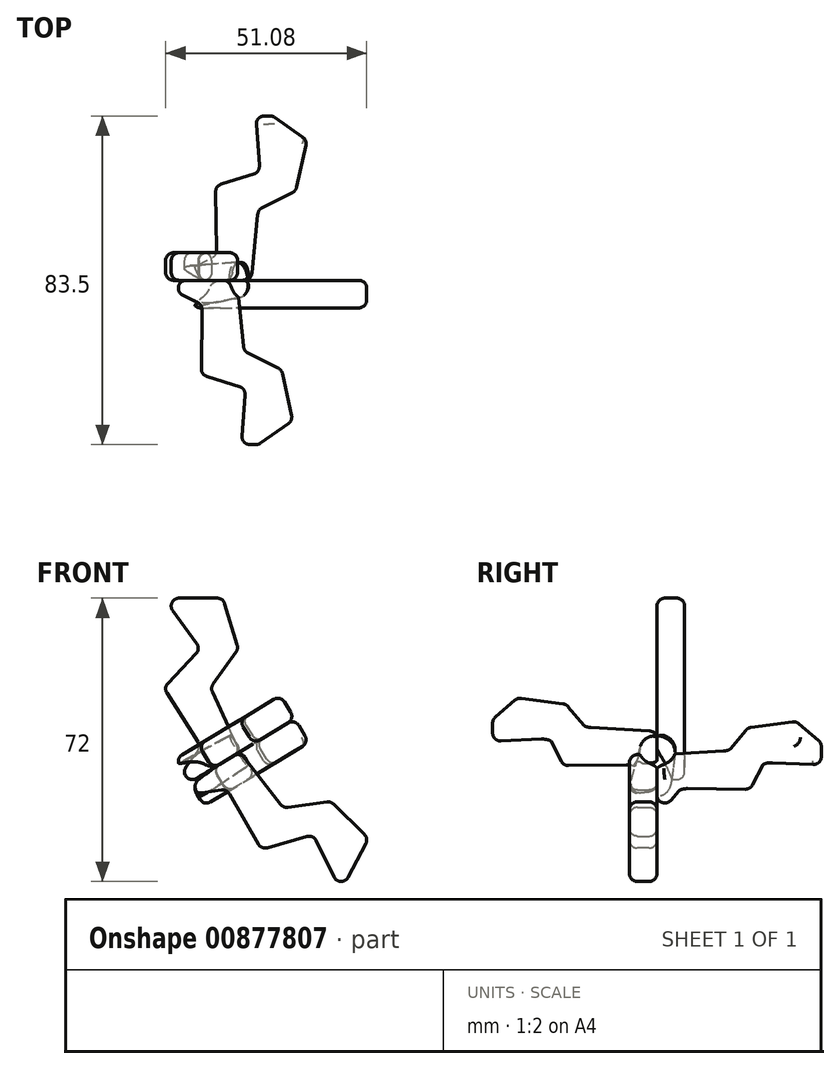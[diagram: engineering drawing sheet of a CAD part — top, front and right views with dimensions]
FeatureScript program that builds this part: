
annotation { "Feature Type Name" : "Feature", "Feature Type Description" : "" }
export const myFeature = defineFeature(function(context is Context, id is Id, definition is map)
    precondition{}
    {
        {
            var Q0;
            Q0=qCreatedBy(makeId("Front.planeOp"),FACE);
            var sketch = newSketch(context, id + "F0", { "sketchPlane" : qUnion([Q0])});
            skLineSegment(sketch, "E0", {"start": v(-48.1, 12.9) * mm, "end": v(-32.98, 12.9) * mm});
            skLineSegment(sketch, "E1", {"start": v(-48.1, 12.9) * mm, "end": v(-38.67, 0) * mm});
            skLineSegment(sketch, "E2", {"start": v(-38.67, 0) * mm, "end": v(-48.1, -9.87) * mm});
            skLineSegment(sketch, "E3", {"start": v(-48.1, -9.87) * mm, "end": v(-38.67, -24.8) * mm});
            skLineSegment(sketch, "E4", {"start": v(-38.67, -24.8) * mm, "end": v(-48.1, -37.96) * mm});
            skLineSegment(sketch, "E5", {"start": v(-48.1, -37.96) * mm, "end": v(-28.71, -26.23) * mm});
            skLineSegment(sketch, "E6", {"start": v(-28.71, -26.23) * mm, "end": v(-36.18, -9.87) * mm});
            skLineSegment(sketch, "E7", {"start": v(-36.18, -9.87) * mm, "end": v(-29.11, 0) * mm});
            skLineSegment(sketch, "E8", {"start": v(-29.11, 0) * mm, "end": v(-32.98, 12.9) * mm});
            skSolve(sketch);
        }
        {
            var Q0;
            Q0=makeQuery(id+"F0.imprint","IMPRINT",FACE,{"disambiguationData":[TD([[makeQuery(id+"F0.imprint","IMPRINT",EDGE,{"derivedFrom":sQuery(id+"F0.wireOp",EDGE,"E0")}),-1.0]])]});
            extrude(context, id + "F1", {"entities" : qUnion([Q0]), "depth" : 7 * mm, "offsetDistance" : 25.4 * mm});
        }
        {
            var Q0;
            Q0=makeQuery(id+"F1.opExtrude","SWEPT_BODY",BODY,{"disambiguationData":[OSD([sQuery(id+"F0.wireOp",EDGE,"E0"),sQuery(id+"F0.wireOp",EDGE,"E1"),sQuery(id+"F0.wireOp",EDGE,"E2"),sQuery(id+"F0.wireOp",EDGE,"E3"),sQuery(id+"F0.wireOp",EDGE,"E4"),sQuery(id+"F0.wireOp",EDGE,"E5"),sQuery(id+"F0.wireOp",EDGE,"E6"),sQuery(id+"F0.wireOp",EDGE,"E7"),sQuery(id+"F0.wireOp",EDGE,"E8")])]});
            var Q1;
            Q1=makeQuery(id+"F1.opExtrude","CAP_EDGE",EDGE,{"disambiguationData":[OSD([sQuery(id+"F0.wireOp",EDGE,"E5")])],"isStart":false});
            circularPattern(context, id + "F2", {"entities" : qUnion([Q0]), "axis" : qUnion([Q1]), "angle" : 360 * degree, "instanceCount" : 4, "equalSpace" : true});
        }
        {
            var Q0;
            Q0=makeQuery(id+"F1.opExtrude","SWEPT_FACE",FACE,{"disambiguationData":[OSD([sQuery(id+"F0.wireOp",EDGE,"E0")])]});
            var Q1;
            Q1=makeQuery(id+"F1.opExtrude","SWEPT_FACE",FACE,{"disambiguationData":[OSD([sQuery(id+"F0.wireOp",EDGE,"E8")])]});
            var Q2;
            Q2=makeQuery(id+"F1.opExtrude","SWEPT_FACE",FACE,{"disambiguationData":[OSD([sQuery(id+"F0.wireOp",EDGE,"E7")])]});
            var Q3;
            Q3=makeQuery(id+"F2.opPattern","COPY",FACE,{"derivedFrom":makeQuery(id+"F1.opExtrude","SWEPT_FACE",FACE,{"disambiguationData":[OSD([sQuery(id+"F0.wireOp",EDGE,"E6")])]}),"instanceName":"1"});
            var Q4;
            Q4=makeQuery(id+"F2.opPattern","COPY",FACE,{"derivedFrom":makeQuery(id+"F1.opExtrude","SWEPT_FACE",FACE,{"disambiguationData":[OSD([sQuery(id+"F0.wireOp",EDGE,"E8")])]}),"instanceName":"1"});
            var Q5;
            Q5=makeQuery(id+"F2.opPattern","COPY",EDGE,{"derivedFrom":makeQuery(id+"F1.opExtrude","SWEPT_EDGE",EDGE,{"disambiguationData":[OSD([sQuery(id+"F0.wireOp",EDGE,"E0"),sQuery(id+"F0.wireOp",EDGE,"E1")])]}),"instanceName":"1"});
            var Q6;
            Q6=makeQuery(id+"F2.opPattern","COPY",FACE,{"derivedFrom":makeQuery(id+"F1.opExtrude","SWEPT_FACE",FACE,{"disambiguationData":[OSD([sQuery(id+"F0.wireOp",EDGE,"E8")])]}),"instanceName":"2"});
            var Q7;
            Q7=makeQuery(id+"F2.opPattern","COPY",FACE,{"derivedFrom":makeQuery(id+"F1.opExtrude","SWEPT_FACE",FACE,{"disambiguationData":[OSD([sQuery(id+"F0.wireOp",EDGE,"E0")])]}),"instanceName":"2"});
            var Q8;
            Q8=makeQuery(id+"F2.opPattern","COPY",FACE,{"derivedFrom":makeQuery(id+"F1.opExtrude","SWEPT_FACE",FACE,{"disambiguationData":[OSD([sQuery(id+"F0.wireOp",EDGE,"E0")])]}),"instanceName":"1"});
            var Q9;
            Q9=makeQuery(id+"F2.opPattern","COPY",FACE,{"derivedFrom":makeQuery(id+"F1.opExtrude","SWEPT_FACE",FACE,{"disambiguationData":[OSD([sQuery(id+"F0.wireOp",EDGE,"E6")])]}),"instanceName":"2"});
            var Q10;
            Q10=makeQuery(id+"F2.opPattern","COPY",FACE,{"derivedFrom":makeQuery(id+"F1.opExtrude","SWEPT_FACE",FACE,{"disambiguationData":[OSD([sQuery(id+"F0.wireOp",EDGE,"E6")])]}),"instanceName":"3"});
            var Q11;
            Q11=makeQuery(id+"F2.opPattern","COPY",FACE,{"derivedFrom":makeQuery(id+"F1.opExtrude","SWEPT_FACE",FACE,{"disambiguationData":[OSD([sQuery(id+"F0.wireOp",EDGE,"E7")])]}),"instanceName":"3"});
            var Q12;
            Q12=makeQuery(id+"F2.opPattern","COPY",FACE,{"derivedFrom":makeQuery(id+"F1.opExtrude","SWEPT_FACE",FACE,{"disambiguationData":[OSD([sQuery(id+"F0.wireOp",EDGE,"E8")])]}),"instanceName":"3"});
            var Q13;
            Q13=makeQuery(id+"F2.opPattern","COPY",EDGE,{"derivedFrom":makeQuery(id+"F1.opExtrude","SWEPT_EDGE",EDGE,{"disambiguationData":[OSD([sQuery(id+"F0.wireOp",EDGE,"E0"),sQuery(id+"F0.wireOp",EDGE,"E1")])]}),"instanceName":"3"});
            var Q14;
            Q14=makeQuery(id+"F2.opPattern","COPY",FACE,{"derivedFrom":makeQuery(id+"F1.opExtrude","CAP_FACE",FACE,{"disambiguationData":[OSD([sQuery(id+"F0.wireOp",EDGE,"E0"),sQuery(id+"F0.wireOp",EDGE,"E1"),sQuery(id+"F0.wireOp",EDGE,"E2"),sQuery(id+"F0.wireOp",EDGE,"E3"),sQuery(id+"F0.wireOp",EDGE,"E4"),sQuery(id+"F0.wireOp",EDGE,"E5"),sQuery(id+"F0.wireOp",EDGE,"E6"),sQuery(id+"F0.wireOp",EDGE,"E7"),sQuery(id+"F0.wireOp",EDGE,"E8")])],"isStart":false}),"instanceName":"2"});
            var Q15;
            Q15=makeQuery(id+"F2.opPattern","COPY",EDGE,{"derivedFrom":makeQuery(id+"F1.opExtrude","CAP_EDGE",EDGE,{"disambiguationData":[OSD([sQuery(id+"F0.wireOp",EDGE,"E1")])],"isStart":false}),"instanceName":"1"});
            var Q16;
            Q16=makeQuery(id+"F1.opExtrude","CAP_FACE",FACE,{"disambiguationData":[OSD([sQuery(id+"F0.wireOp",EDGE,"E0"),sQuery(id+"F0.wireOp",EDGE,"E1"),sQuery(id+"F0.wireOp",EDGE,"E2"),sQuery(id+"F0.wireOp",EDGE,"E3"),sQuery(id+"F0.wireOp",EDGE,"E4"),sQuery(id+"F0.wireOp",EDGE,"E5"),sQuery(id+"F0.wireOp",EDGE,"E6"),sQuery(id+"F0.wireOp",EDGE,"E7"),sQuery(id+"F0.wireOp",EDGE,"E8")])],"isStart":true});
            var Q17;
            Q17=makeQuery(id+"F2.opPattern","COPY",FACE,{"derivedFrom":makeQuery(id+"F1.opExtrude","CAP_FACE",FACE,{"disambiguationData":[OSD([sQuery(id+"F0.wireOp",EDGE,"E0"),sQuery(id+"F0.wireOp",EDGE,"E1"),sQuery(id+"F0.wireOp",EDGE,"E2"),sQuery(id+"F0.wireOp",EDGE,"E3"),sQuery(id+"F0.wireOp",EDGE,"E4"),sQuery(id+"F0.wireOp",EDGE,"E5"),sQuery(id+"F0.wireOp",EDGE,"E6"),sQuery(id+"F0.wireOp",EDGE,"E7"),sQuery(id+"F0.wireOp",EDGE,"E8")])],"isStart":true}),"instanceName":"3"});
            var Q18;
            Q18=makeQuery(id+"F1.opExtrude","CAP_FACE",FACE,{"disambiguationData":[OSD([sQuery(id+"F0.wireOp",EDGE,"E0"),sQuery(id+"F0.wireOp",EDGE,"E1"),sQuery(id+"F0.wireOp",EDGE,"E2"),sQuery(id+"F0.wireOp",EDGE,"E3"),sQuery(id+"F0.wireOp",EDGE,"E4"),sQuery(id+"F0.wireOp",EDGE,"E5"),sQuery(id+"F0.wireOp",EDGE,"E6"),sQuery(id+"F0.wireOp",EDGE,"E7"),sQuery(id+"F0.wireOp",EDGE,"E8")])],"isStart":false});
            var Q19;
            Q19=makeQuery(id+"F2.opPattern","COPY",FACE,{"derivedFrom":makeQuery(id+"F1.opExtrude","CAP_FACE",FACE,{"disambiguationData":[OSD([sQuery(id+"F0.wireOp",EDGE,"E0"),sQuery(id+"F0.wireOp",EDGE,"E1"),sQuery(id+"F0.wireOp",EDGE,"E2"),sQuery(id+"F0.wireOp",EDGE,"E3"),sQuery(id+"F0.wireOp",EDGE,"E4"),sQuery(id+"F0.wireOp",EDGE,"E5"),sQuery(id+"F0.wireOp",EDGE,"E6"),sQuery(id+"F0.wireOp",EDGE,"E7"),sQuery(id+"F0.wireOp",EDGE,"E8")])],"isStart":true}),"instanceName":"1"});
            var Q20;
            Q20=makeQuery(id+"F2.opPattern","COPY",FACE,{"derivedFrom":makeQuery(id+"F1.opExtrude","CAP_FACE",FACE,{"disambiguationData":[OSD([sQuery(id+"F0.wireOp",EDGE,"E0"),sQuery(id+"F0.wireOp",EDGE,"E1"),sQuery(id+"F0.wireOp",EDGE,"E2"),sQuery(id+"F0.wireOp",EDGE,"E3"),sQuery(id+"F0.wireOp",EDGE,"E4"),sQuery(id+"F0.wireOp",EDGE,"E5"),sQuery(id+"F0.wireOp",EDGE,"E6"),sQuery(id+"F0.wireOp",EDGE,"E7"),sQuery(id+"F0.wireOp",EDGE,"E8")])],"isStart":false}),"instanceName":"1"});
            var Q21;
            Q21=makeQuery(id+"F2.opPattern","COPY",EDGE,{"derivedFrom":makeQuery(id+"F1.opExtrude","CAP_EDGE",EDGE,{"disambiguationData":[OSD([sQuery(id+"F0.wireOp",EDGE,"E8")])],"isStart":false}),"instanceName":"1"});
            var Q22;
            Q22=makeQuery(id+"F2.opPattern","COPY",EDGE,{"derivedFrom":makeQuery(id+"F1.opExtrude","CAP_EDGE",EDGE,{"disambiguationData":[OSD([sQuery(id+"F0.wireOp",EDGE,"E0")])],"isStart":false}),"instanceName":"1"});
            var Q23;
            Q23=makeQuery(id+"F2.opPattern","COPY",EDGE,{"derivedFrom":makeQuery(id+"F1.opExtrude","SWEPT_EDGE",EDGE,{"disambiguationData":[OSD([sQuery(id+"F0.wireOp",EDGE,"E6"),sQuery(id+"F0.wireOp",EDGE,"E7")])]}),"instanceName":"1"});
            var Q24;
            Q24=makeQuery(id+"F2.opPattern","COPY",EDGE,{"derivedFrom":makeQuery(id+"F1.opExtrude","CAP_EDGE",EDGE,{"disambiguationData":[OSD([sQuery(id+"F0.wireOp",EDGE,"E6")])],"isStart":true}),"instanceName":"1"});
            var Q25;
            Q25=makeQuery(id+"F2.opPattern","COPY",EDGE,{"derivedFrom":makeQuery(id+"F1.opExtrude","SWEPT_EDGE",EDGE,{"disambiguationData":[OSD([sQuery(id+"F0.wireOp",EDGE,"E0"),sQuery(id+"F0.wireOp",EDGE,"E8")])]}),"instanceName":"1"});
            var Q26;
            Q26=makeQuery(id+"F2.opPattern","COPY",EDGE,{"derivedFrom":makeQuery(id+"F1.opExtrude","CAP_EDGE",EDGE,{"disambiguationData":[OSD([sQuery(id+"F0.wireOp",EDGE,"E6")])],"isStart":false}),"instanceName":"1"});
            var Q27;
            Q27=makeQuery(id+"F2.opPattern","COPY",EDGE,{"derivedFrom":makeQuery(id+"F1.opExtrude","CAP_EDGE",EDGE,{"disambiguationData":[OSD([sQuery(id+"F0.wireOp",EDGE,"E8")])],"isStart":true}),"instanceName":"1"});
            var Q28;
            Q28=makeQuery(id+"F2.opPattern","COPY",EDGE,{"derivedFrom":makeQuery(id+"F1.opExtrude","SWEPT_EDGE",EDGE,{"disambiguationData":[OSD([sQuery(id+"F0.wireOp",EDGE,"E7"),sQuery(id+"F0.wireOp",EDGE,"E8")])]}),"instanceName":"1"});
            var Q29;
            Q29=makeQuery(id+"F2.opPattern","COPY",EDGE,{"derivedFrom":makeQuery(id+"F1.opExtrude","CAP_EDGE",EDGE,{"disambiguationData":[OSD([sQuery(id+"F0.wireOp",EDGE,"E6")])],"isStart":false}),"instanceName":"2"});
            var Q30;
            Q30=makeQuery(id+"F2.opPattern","COPY",EDGE,{"derivedFrom":makeQuery(id+"F1.opExtrude","CAP_EDGE",EDGE,{"disambiguationData":[OSD([sQuery(id+"F0.wireOp",EDGE,"E4")])],"isStart":false}),"instanceName":"2"});
            var Q31;
            Q31=makeQuery(id+"F2.opPattern","COPY",EDGE,{"derivedFrom":makeQuery(id+"F1.opExtrude","CAP_EDGE",EDGE,{"disambiguationData":[OSD([sQuery(id+"F0.wireOp",EDGE,"E0")])],"isStart":true}),"instanceName":"2"});
            var Q32;
            Q32=makeQuery(id+"F2.opPattern","COPY",EDGE,{"derivedFrom":makeQuery(id+"F1.opExtrude","SWEPT_EDGE",EDGE,{"disambiguationData":[OSD([sQuery(id+"F0.wireOp",EDGE,"E4"),sQuery(id+"F0.wireOp",EDGE,"E5")])]}),"instanceName":"2"});
            var Q33;
            Q33=makeQuery(id+"F2.opPattern","COPY",EDGE,{"derivedFrom":makeQuery(id+"F1.opExtrude","CAP_EDGE",EDGE,{"disambiguationData":[OSD([sQuery(id+"F0.wireOp",EDGE,"E0")])],"isStart":false}),"instanceName":"2"});
            var Q34;
            Q34=makeQuery(id+"F2.opPattern","COPY",EDGE,{"derivedFrom":makeQuery(id+"F1.opExtrude","SWEPT_EDGE",EDGE,{"disambiguationData":[OSD([sQuery(id+"F0.wireOp",EDGE,"E0"),sQuery(id+"F0.wireOp",EDGE,"E1")])]}),"instanceName":"2"});
            var Q35;
            Q35=makeQuery(id+"F2.opPattern","COPY",EDGE,{"derivedFrom":makeQuery(id+"F1.opExtrude","SWEPT_EDGE",EDGE,{"disambiguationData":[OSD([sQuery(id+"F0.wireOp",EDGE,"E2"),sQuery(id+"F0.wireOp",EDGE,"E3")])]}),"instanceName":"2"});
            var Q36;
            Q36=makeQuery(id+"F2.opPattern","COPY",EDGE,{"derivedFrom":makeQuery(id+"F1.opExtrude","SWEPT_EDGE",EDGE,{"disambiguationData":[OSD([sQuery(id+"F0.wireOp",EDGE,"E5"),sQuery(id+"F0.wireOp",EDGE,"E6")])]}),"instanceName":"2"});
            var Q37;
            Q37=makeQuery(id+"F2.opPattern","COPY",EDGE,{"derivedFrom":makeQuery(id+"F1.opExtrude","CAP_EDGE",EDGE,{"disambiguationData":[OSD([sQuery(id+"F0.wireOp",EDGE,"E4")])],"isStart":true}),"instanceName":"2"});
            var Q38;
            Q38=makeQuery(id+"F2.opPattern","COPY",EDGE,{"derivedFrom":makeQuery(id+"F1.opExtrude","CAP_EDGE",EDGE,{"disambiguationData":[OSD([sQuery(id+"F0.wireOp",EDGE,"E7")])],"isStart":false}),"instanceName":"2"});
            var Q39;
            Q39=makeQuery(id+"F2.opPattern","COPY",EDGE,{"derivedFrom":makeQuery(id+"F1.opExtrude","CAP_EDGE",EDGE,{"disambiguationData":[OSD([sQuery(id+"F0.wireOp",EDGE,"E2")])],"isStart":true}),"instanceName":"2"});
            var Q40;
            Q40=makeQuery(id+"F1.opExtrude","CAP_EDGE",EDGE,{"disambiguationData":[OSD([sQuery(id+"F0.wireOp",EDGE,"E5")])],"isStart":true});
            var Q41;
            Q41=makeQuery(id+"F1.opExtrude","SWEPT_EDGE",EDGE,{"disambiguationData":[OSD([sQuery(id+"F0.wireOp",EDGE,"E4"),sQuery(id+"F0.wireOp",EDGE,"E5")])]});
            var Q42;
            Q42=makeQuery(id+"F1.opExtrude","CAP_EDGE",EDGE,{"disambiguationData":[OSD([sQuery(id+"F0.wireOp",EDGE,"E4")])],"isStart":true});
            var Q43;
            Q43=makeQuery(id+"F1.opExtrude","SWEPT_EDGE",EDGE,{"disambiguationData":[OSD([sQuery(id+"F0.wireOp",EDGE,"E2"),sQuery(id+"F0.wireOp",EDGE,"E3")])]});
            var Q44;
            Q44=makeQuery(id+"F1.opExtrude","SWEPT_EDGE",EDGE,{"disambiguationData":[OSD([sQuery(id+"F0.wireOp",EDGE,"E3"),sQuery(id+"F0.wireOp",EDGE,"E4")])]});
            var Q45;
            Q45=makeQuery(id+"F1.opExtrude","SWEPT_EDGE",EDGE,{"disambiguationData":[OSD([sQuery(id+"F0.wireOp",EDGE,"E6"),sQuery(id+"F0.wireOp",EDGE,"E7")])]});
            var Q46;
            Q46=makeQuery(id+"F1.opExtrude","CAP_EDGE",EDGE,{"disambiguationData":[OSD([sQuery(id+"F0.wireOp",EDGE,"E5")])],"isStart":false});
            var Q47;
            Q47=makeQuery(id+"F2.opPattern","COPY",EDGE,{"derivedFrom":makeQuery(id+"F1.opExtrude","SWEPT_EDGE",EDGE,{"disambiguationData":[OSD([sQuery(id+"F0.wireOp",EDGE,"E4"),sQuery(id+"F0.wireOp",EDGE,"E5")])]}),"instanceName":"3"});
            var Q48;
            Q48=makeQuery(id+"F2.opPattern","COPY",EDGE,{"derivedFrom":makeQuery(id+"F1.opExtrude","CAP_EDGE",EDGE,{"disambiguationData":[OSD([sQuery(id+"F0.wireOp",EDGE,"E6")])],"isStart":false}),"instanceName":"3"});
            var Q49;
            Q49=makeQuery(id+"F2.opPattern","COPY",EDGE,{"derivedFrom":makeQuery(id+"F1.opExtrude","SWEPT_EDGE",EDGE,{"disambiguationData":[OSD([sQuery(id+"F0.wireOp",EDGE,"E3"),sQuery(id+"F0.wireOp",EDGE,"E4")])]}),"instanceName":"3"});
            var Q50;
            Q50=makeQuery(id+"F2.opPattern","COPY",EDGE,{"derivedFrom":makeQuery(id+"F1.opExtrude","CAP_EDGE",EDGE,{"disambiguationData":[OSD([sQuery(id+"F0.wireOp",EDGE,"E3")])],"isStart":true}),"instanceName":"3"});
            var Q51;
            Q51=makeQuery(id+"F2.opPattern","COPY",EDGE,{"derivedFrom":makeQuery(id+"F1.opExtrude","CAP_EDGE",EDGE,{"disambiguationData":[OSD([sQuery(id+"F0.wireOp",EDGE,"E6")])],"isStart":true}),"instanceName":"3"});
            var Q52;
            Q52=makeQuery(id+"F2.opPattern","COPY",EDGE,{"derivedFrom":makeQuery(id+"F1.opExtrude","CAP_EDGE",EDGE,{"disambiguationData":[OSD([sQuery(id+"F0.wireOp",EDGE,"E4")])],"isStart":false}),"instanceName":"3"});
            var Q53;
            Q53=makeQuery(id+"F2.opPattern","COPY",EDGE,{"derivedFrom":makeQuery(id+"F1.opExtrude","CAP_EDGE",EDGE,{"disambiguationData":[OSD([sQuery(id+"F0.wireOp",EDGE,"E7")])],"isStart":true}),"instanceName":"3"});
            var Q54;
            Q54=makeQuery(id+"F2.opPattern","COPY",EDGE,{"derivedFrom":makeQuery(id+"F1.opExtrude","SWEPT_EDGE",EDGE,{"disambiguationData":[OSD([sQuery(id+"F0.wireOp",EDGE,"E2"),sQuery(id+"F0.wireOp",EDGE,"E3")])]}),"instanceName":"3"});
            var Q55;
            Q55=makeQuery(id+"F2.opPattern","COPY",EDGE,{"derivedFrom":makeQuery(id+"F1.opExtrude","SWEPT_EDGE",EDGE,{"disambiguationData":[OSD([sQuery(id+"F0.wireOp",EDGE,"E5"),sQuery(id+"F0.wireOp",EDGE,"E6")])]}),"instanceName":"3"});
            var Q56;
            Q56=makeQuery(id+"F2.opPattern","COPY",EDGE,{"derivedFrom":makeQuery(id+"F1.opExtrude","SWEPT_EDGE",EDGE,{"disambiguationData":[OSD([sQuery(id+"F0.wireOp",EDGE,"E6"),sQuery(id+"F0.wireOp",EDGE,"E7")])]}),"instanceName":"3"});
            var Q57;
            Q57=makeQuery(id+"F2.opPattern","COPY",EDGE,{"derivedFrom":makeQuery(id+"F1.opExtrude","CAP_EDGE",EDGE,{"disambiguationData":[OSD([sQuery(id+"F0.wireOp",EDGE,"E5")])],"isStart":true}),"instanceName":"3"});
            var Q58;
            Q58=makeQuery(id+"F2.opPattern","COPY",EDGE,{"derivedFrom":makeQuery(id+"F1.opExtrude","CAP_EDGE",EDGE,{"disambiguationData":[OSD([sQuery(id+"F0.wireOp",EDGE,"E2")])],"isStart":true}),"instanceName":"3"});
            var Q59;
            Q59=makeQuery(id+"F2.opPattern","COPY",EDGE,{"derivedFrom":makeQuery(id+"F1.opExtrude","CAP_EDGE",EDGE,{"disambiguationData":[OSD([sQuery(id+"F0.wireOp",EDGE,"E4")])],"isStart":true}),"instanceName":"3"});
            var Q60;
            Q60=makeQuery(id+"F2.opPattern","COPY",EDGE,{"derivedFrom":makeQuery(id+"F1.opExtrude","SWEPT_EDGE",EDGE,{"disambiguationData":[OSD([sQuery(id+"F0.wireOp",EDGE,"E5"),sQuery(id+"F0.wireOp",EDGE,"E6")])]}),"instanceName":"1"});
            var Q61;
            Q61=makeQuery(id+"F2.opPattern","COPY",EDGE,{"derivedFrom":makeQuery(id+"F1.opExtrude","CAP_EDGE",EDGE,{"disambiguationData":[OSD([sQuery(id+"F0.wireOp",EDGE,"E7")])],"isStart":true}),"instanceName":"1"});
            var Q62;
            Q62=makeQuery(id+"F2.opPattern","COPY",EDGE,{"derivedFrom":makeQuery(id+"F1.opExtrude","CAP_EDGE",EDGE,{"disambiguationData":[OSD([sQuery(id+"F0.wireOp",EDGE,"E5")])],"isStart":true}),"instanceName":"1"});
            var Q63;
            Q63=makeQuery(id+"F2.opPattern","COPY",EDGE,{"derivedFrom":makeQuery(id+"F1.opExtrude","CAP_EDGE",EDGE,{"disambiguationData":[OSD([sQuery(id+"F0.wireOp",EDGE,"E7")])],"isStart":false}),"instanceName":"1"});
            var Q64;
            Q64=makeQuery(id+"F2.opPattern","COPY",EDGE,{"derivedFrom":makeQuery(id+"F1.opExtrude","CAP_EDGE",EDGE,{"disambiguationData":[OSD([sQuery(id+"F0.wireOp",EDGE,"E5")])],"isStart":false}),"instanceName":"1"});
            var Q65;
            Q65=makeQuery(id+"F2.opPattern","COPY",EDGE,{"derivedFrom":makeQuery(id+"F1.opExtrude","CAP_EDGE",EDGE,{"disambiguationData":[OSD([sQuery(id+"F0.wireOp",EDGE,"E2")])],"isStart":true}),"instanceName":"1"});
            var Q66;
            Q66=makeQuery(id+"F2.opPattern","COPY",EDGE,{"derivedFrom":makeQuery(id+"F1.opExtrude","CAP_EDGE",EDGE,{"disambiguationData":[OSD([sQuery(id+"F0.wireOp",EDGE,"E1")])],"isStart":true}),"instanceName":"1"});
            var Q67;
            Q67=makeQuery(id+"F2.opPattern","COPY",EDGE,{"derivedFrom":makeQuery(id+"F1.opExtrude","CAP_EDGE",EDGE,{"disambiguationData":[OSD([sQuery(id+"F0.wireOp",EDGE,"E3")])],"isStart":true}),"instanceName":"1"});
            var Q68;
            Q68=makeQuery(id+"F2.opPattern","COPY",EDGE,{"derivedFrom":makeQuery(id+"F1.opExtrude","SWEPT_EDGE",EDGE,{"disambiguationData":[OSD([sQuery(id+"F0.wireOp",EDGE,"E2"),sQuery(id+"F0.wireOp",EDGE,"E3")])]}),"instanceName":"1"});
            var Q69;
            Q69=makeQuery(id+"F2.opPattern","COPY",EDGE,{"derivedFrom":makeQuery(id+"F1.opExtrude","CAP_EDGE",EDGE,{"disambiguationData":[OSD([sQuery(id+"F0.wireOp",EDGE,"E0")])],"isStart":true}),"instanceName":"1"});
            var Q70;
            Q70=makeQuery(id+"F2.opPattern","COPY",EDGE,{"derivedFrom":makeQuery(id+"F1.opExtrude","SWEPT_EDGE",EDGE,{"disambiguationData":[OSD([sQuery(id+"F0.wireOp",EDGE,"E1"),sQuery(id+"F0.wireOp",EDGE,"E2")])]}),"instanceName":"1"});
            var Q71;
            Q71=makeQuery(id+"F2.opPattern","COPY",EDGE,{"derivedFrom":makeQuery(id+"F1.opExtrude","CAP_EDGE",EDGE,{"disambiguationData":[OSD([sQuery(id+"F0.wireOp",EDGE,"E3")])],"isStart":false}),"instanceName":"1"});
            var Q72;
            Q72=makeQuery(id+"F2.opPattern","COPY",EDGE,{"derivedFrom":makeQuery(id+"F1.opExtrude","SWEPT_EDGE",EDGE,{"disambiguationData":[OSD([sQuery(id+"F0.wireOp",EDGE,"E3"),sQuery(id+"F0.wireOp",EDGE,"E4")])]}),"instanceName":"1"});
            var Q73;
            Q73=makeQuery(id+"F2.opPattern","COPY",EDGE,{"derivedFrom":makeQuery(id+"F1.opExtrude","SWEPT_EDGE",EDGE,{"disambiguationData":[OSD([sQuery(id+"F0.wireOp",EDGE,"E4"),sQuery(id+"F0.wireOp",EDGE,"E5")])]}),"instanceName":"1"});
            var Q74;
            Q74=makeQuery(id+"F2.opPattern","COPY",EDGE,{"derivedFrom":makeQuery(id+"F1.opExtrude","CAP_EDGE",EDGE,{"disambiguationData":[OSD([sQuery(id+"F0.wireOp",EDGE,"E3")])],"isStart":true}),"instanceName":"2"});
            var Q75;
            Q75=makeQuery(id+"F2.opPattern","COPY",EDGE,{"derivedFrom":makeQuery(id+"F1.opExtrude","CAP_EDGE",EDGE,{"disambiguationData":[OSD([sQuery(id+"F0.wireOp",EDGE,"E8")])],"isStart":true}),"instanceName":"2"});
            var Q76;
            Q76=makeQuery(id+"F2.opPattern","COPY",EDGE,{"derivedFrom":makeQuery(id+"F1.opExtrude","CAP_EDGE",EDGE,{"disambiguationData":[OSD([sQuery(id+"F0.wireOp",EDGE,"E5")])],"isStart":true}),"instanceName":"2"});
            var Q77;
            Q77=makeQuery(id+"F2.opPattern","COPY",EDGE,{"derivedFrom":makeQuery(id+"F1.opExtrude","CAP_EDGE",EDGE,{"disambiguationData":[OSD([sQuery(id+"F0.wireOp",EDGE,"E1")])],"isStart":false}),"instanceName":"2"});
            var Q78;
            Q78=makeQuery(id+"F2.opPattern","COPY",EDGE,{"derivedFrom":makeQuery(id+"F1.opExtrude","SWEPT_EDGE",EDGE,{"disambiguationData":[OSD([sQuery(id+"F0.wireOp",EDGE,"E3"),sQuery(id+"F0.wireOp",EDGE,"E4")])]}),"instanceName":"2"});
            var Q79;
            Q79=makeQuery(id+"F2.opPattern","COPY",EDGE,{"derivedFrom":makeQuery(id+"F1.opExtrude","SWEPT_EDGE",EDGE,{"disambiguationData":[OSD([sQuery(id+"F0.wireOp",EDGE,"E6"),sQuery(id+"F0.wireOp",EDGE,"E7")])]}),"instanceName":"2"});
            var Q80;
            Q80=makeQuery(id+"F2.opPattern","COPY",EDGE,{"derivedFrom":makeQuery(id+"F1.opExtrude","CAP_EDGE",EDGE,{"disambiguationData":[OSD([sQuery(id+"F0.wireOp",EDGE,"E6")])],"isStart":true}),"instanceName":"2"});
            var Q81;
            Q81=makeQuery(id+"F2.opPattern","COPY",EDGE,{"derivedFrom":makeQuery(id+"F1.opExtrude","SWEPT_EDGE",EDGE,{"disambiguationData":[OSD([sQuery(id+"F0.wireOp",EDGE,"E1"),sQuery(id+"F0.wireOp",EDGE,"E2")])]}),"instanceName":"2"});
            var Q82;
            Q82=makeQuery(id+"F2.opPattern","COPY",EDGE,{"derivedFrom":makeQuery(id+"F1.opExtrude","SWEPT_EDGE",EDGE,{"disambiguationData":[OSD([sQuery(id+"F0.wireOp",EDGE,"E0"),sQuery(id+"F0.wireOp",EDGE,"E8")])]}),"instanceName":"2"});
            var Q83;
            Q83=makeQuery(id+"F2.opPattern","COPY",EDGE,{"derivedFrom":makeQuery(id+"F1.opExtrude","CAP_EDGE",EDGE,{"disambiguationData":[OSD([sQuery(id+"F0.wireOp",EDGE,"E2")])],"isStart":false}),"instanceName":"2"});
            var Q84;
            Q84=makeQuery(id+"F2.opPattern","COPY",EDGE,{"derivedFrom":makeQuery(id+"F1.opExtrude","CAP_EDGE",EDGE,{"disambiguationData":[OSD([sQuery(id+"F0.wireOp",EDGE,"E7")])],"isStart":true}),"instanceName":"2"});
            var Q85;
            Q85=makeQuery(id+"F2.opPattern","COPY",EDGE,{"derivedFrom":makeQuery(id+"F1.opExtrude","CAP_EDGE",EDGE,{"disambiguationData":[OSD([sQuery(id+"F0.wireOp",EDGE,"E3")])],"isStart":false}),"instanceName":"2"});
            var Q86;
            Q86=makeQuery(id+"F2.opPattern","COPY",EDGE,{"derivedFrom":makeQuery(id+"F1.opExtrude","CAP_EDGE",EDGE,{"disambiguationData":[OSD([sQuery(id+"F0.wireOp",EDGE,"E8")])],"isStart":false}),"instanceName":"2"});
            var Q87;
            Q87=makeQuery(id+"F2.opPattern","COPY",EDGE,{"derivedFrom":makeQuery(id+"F1.opExtrude","CAP_EDGE",EDGE,{"disambiguationData":[OSD([sQuery(id+"F0.wireOp",EDGE,"E1")])],"isStart":true}),"instanceName":"2"});
            var Q88;
            Q88=makeQuery(id+"F1.opExtrude","CAP_EDGE",EDGE,{"disambiguationData":[OSD([sQuery(id+"F0.wireOp",EDGE,"E6")])],"isStart":true});
            var Q89;
            Q89=makeQuery(id+"F1.opExtrude","CAP_EDGE",EDGE,{"disambiguationData":[OSD([sQuery(id+"F0.wireOp",EDGE,"E6")])],"isStart":false});
            var Q90;
            Q90=makeQuery(id+"F1.opExtrude","SWEPT_EDGE",EDGE,{"disambiguationData":[OSD([sQuery(id+"F0.wireOp",EDGE,"E5"),sQuery(id+"F0.wireOp",EDGE,"E6")])]});
            var Q91;
            Q91=makeQuery(id+"F1.opExtrude","CAP_EDGE",EDGE,{"disambiguationData":[OSD([sQuery(id+"F0.wireOp",EDGE,"E3")])],"isStart":false});
            var Q92;
            Q92=makeQuery(id+"F1.opExtrude","CAP_EDGE",EDGE,{"disambiguationData":[OSD([sQuery(id+"F0.wireOp",EDGE,"E4")])],"isStart":false});
            var Q93;
            Q93=makeQuery(id+"F1.opExtrude","CAP_EDGE",EDGE,{"disambiguationData":[OSD([sQuery(id+"F0.wireOp",EDGE,"E3")])],"isStart":true});
            var Q94;
            Q94=makeQuery(id+"F2.opPattern","COPY",EDGE,{"derivedFrom":makeQuery(id+"F1.opExtrude","CAP_EDGE",EDGE,{"disambiguationData":[OSD([sQuery(id+"F0.wireOp",EDGE,"E3")])],"isStart":false}),"instanceName":"3"});
            var Q95;
            Q95=makeQuery(id+"F2.opPattern","COPY",EDGE,{"derivedFrom":makeQuery(id+"F1.opExtrude","CAP_EDGE",EDGE,{"disambiguationData":[OSD([sQuery(id+"F0.wireOp",EDGE,"E4")])],"isStart":false}),"instanceName":"1"});
            var Q96;
            Q96=makeQuery(id+"F2.opPattern","COPY",EDGE,{"derivedFrom":makeQuery(id+"F1.opExtrude","CAP_EDGE",EDGE,{"disambiguationData":[OSD([sQuery(id+"F0.wireOp",EDGE,"E2")])],"isStart":false}),"instanceName":"1"});
            var Q97;
            Q97=makeQuery(id+"F2.opPattern","COPY",EDGE,{"derivedFrom":makeQuery(id+"F1.opExtrude","CAP_EDGE",EDGE,{"disambiguationData":[OSD([sQuery(id+"F0.wireOp",EDGE,"E4")])],"isStart":true}),"instanceName":"1"});
            var Q98;
            Q98=makeQuery(id+"F2.opPattern","COPY",EDGE,{"derivedFrom":makeQuery(id+"F1.opExtrude","CAP_EDGE",EDGE,{"disambiguationData":[OSD([sQuery(id+"F0.wireOp",EDGE,"E5")])],"isStart":false}),"instanceName":"2"});
            var Q99;
            Q99=makeQuery(id+"F2.opPattern","COPY",EDGE,{"derivedFrom":makeQuery(id+"F1.opExtrude","SWEPT_EDGE",EDGE,{"disambiguationData":[OSD([sQuery(id+"F0.wireOp",EDGE,"E7"),sQuery(id+"F0.wireOp",EDGE,"E8")])]}),"instanceName":"2"});
            var Q100;
            Q100=makeQuery(id+"F2.opPattern","COPY",EDGE,{"derivedFrom":makeQuery(id+"F1.opExtrude","CAP_EDGE",EDGE,{"disambiguationData":[OSD([sQuery(id+"F0.wireOp",EDGE,"E5")])],"isStart":false}),"instanceName":"3"});
            var Q101;
            Q101=makeQuery(id+"F1.opExtrude","SWEPT_EDGE",EDGE,{"disambiguationData":[OSD([sQuery(id+"F0.wireOp",EDGE,"E0"),sQuery(id+"F0.wireOp",EDGE,"E8")])]});
            var Q102;
            Q102=makeQuery(id+"F1.opExtrude","CAP_EDGE",EDGE,{"disambiguationData":[OSD([sQuery(id+"F0.wireOp",EDGE,"E7")])],"isStart":true});
            var Q103;
            Q103=makeQuery(id+"F1.opExtrude","SWEPT_EDGE",EDGE,{"disambiguationData":[OSD([sQuery(id+"F0.wireOp",EDGE,"E7"),sQuery(id+"F0.wireOp",EDGE,"E8")])]});
            var Q104;
            Q104=makeQuery(id+"F1.opExtrude","CAP_EDGE",EDGE,{"disambiguationData":[OSD([sQuery(id+"F0.wireOp",EDGE,"E7")])],"isStart":false});
            var Q105;
            Q105=makeQuery(id+"F2.opPattern","COPY",EDGE,{"derivedFrom":makeQuery(id+"F1.opExtrude","SWEPT_EDGE",EDGE,{"disambiguationData":[OSD([sQuery(id+"F0.wireOp",EDGE,"E7"),sQuery(id+"F0.wireOp",EDGE,"E8")])]}),"instanceName":"3"});
            var Q106;
            Q106=makeQuery(id+"F2.opPattern","COPY",EDGE,{"derivedFrom":makeQuery(id+"F1.opExtrude","SWEPT_EDGE",EDGE,{"disambiguationData":[OSD([sQuery(id+"F0.wireOp",EDGE,"E0"),sQuery(id+"F0.wireOp",EDGE,"E8")])]}),"instanceName":"3"});
            var Q107;
            Q107=makeQuery(id+"F2.opPattern","COPY",EDGE,{"derivedFrom":makeQuery(id+"F1.opExtrude","CAP_EDGE",EDGE,{"disambiguationData":[OSD([sQuery(id+"F0.wireOp",EDGE,"E8")])],"isStart":true}),"instanceName":"3"});
            var Q108;
            Q108=makeQuery(id+"F2.opPattern","COPY",EDGE,{"derivedFrom":makeQuery(id+"F1.opExtrude","CAP_EDGE",EDGE,{"disambiguationData":[OSD([sQuery(id+"F0.wireOp",EDGE,"E1")])],"isStart":true}),"instanceName":"3"});
            var Q109;
            Q109=makeQuery(id+"F2.opPattern","COPY",EDGE,{"derivedFrom":makeQuery(id+"F1.opExtrude","CAP_EDGE",EDGE,{"disambiguationData":[OSD([sQuery(id+"F0.wireOp",EDGE,"E2")])],"isStart":false}),"instanceName":"3"});
            var Q110;
            Q110=makeQuery(id+"F1.opExtrude","CAP_EDGE",EDGE,{"disambiguationData":[OSD([sQuery(id+"F0.wireOp",EDGE,"E8")])],"isStart":false});
            var Q111;
            Q111=makeQuery(id+"F1.opExtrude","CAP_EDGE",EDGE,{"disambiguationData":[OSD([sQuery(id+"F0.wireOp",EDGE,"E0")])],"isStart":false});
            var Q112;
            Q112=makeQuery(id+"F1.opExtrude","CAP_EDGE",EDGE,{"disambiguationData":[OSD([sQuery(id+"F0.wireOp",EDGE,"E1")])],"isStart":true});
            var Q113;
            Q113=makeQuery(id+"F1.opExtrude","SWEPT_EDGE",EDGE,{"disambiguationData":[OSD([sQuery(id+"F0.wireOp",EDGE,"E0"),sQuery(id+"F0.wireOp",EDGE,"E1")])]});
            var Q114;
            Q114=makeQuery(id+"F1.opExtrude","CAP_EDGE",EDGE,{"disambiguationData":[OSD([sQuery(id+"F0.wireOp",EDGE,"E1")])],"isStart":false});
            var Q115;
            Q115=makeQuery(id+"F1.opExtrude","SWEPT_EDGE",EDGE,{"disambiguationData":[OSD([sQuery(id+"F0.wireOp",EDGE,"E1"),sQuery(id+"F0.wireOp",EDGE,"E2")])]});
            var Q116;
            Q116=makeQuery(id+"F1.opExtrude","CAP_EDGE",EDGE,{"disambiguationData":[OSD([sQuery(id+"F0.wireOp",EDGE,"E0")])],"isStart":true});
            var Q117;
            Q117=makeQuery(id+"F1.opExtrude","CAP_EDGE",EDGE,{"disambiguationData":[OSD([sQuery(id+"F0.wireOp",EDGE,"E8")])],"isStart":true});
            var Q118;
            Q118=makeQuery(id+"F2.opPattern","COPY",EDGE,{"derivedFrom":makeQuery(id+"F1.opExtrude","CAP_EDGE",EDGE,{"disambiguationData":[OSD([sQuery(id+"F0.wireOp",EDGE,"E1")])],"isStart":false}),"instanceName":"3"});
            var Q119;
            Q119=makeQuery(id+"F2.opPattern","COPY",EDGE,{"derivedFrom":makeQuery(id+"F1.opExtrude","CAP_EDGE",EDGE,{"disambiguationData":[OSD([sQuery(id+"F0.wireOp",EDGE,"E8")])],"isStart":false}),"instanceName":"3"});
            var Q120;
            Q120=makeQuery(id+"F2.opPattern","COPY",EDGE,{"derivedFrom":makeQuery(id+"F1.opExtrude","CAP_EDGE",EDGE,{"disambiguationData":[OSD([sQuery(id+"F0.wireOp",EDGE,"E0")])],"isStart":true}),"instanceName":"3"});
            var Q121;
            Q121=makeQuery(id+"F2.opPattern","COPY",EDGE,{"derivedFrom":makeQuery(id+"F1.opExtrude","CAP_EDGE",EDGE,{"disambiguationData":[OSD([sQuery(id+"F0.wireOp",EDGE,"E0")])],"isStart":false}),"instanceName":"3"});
            var Q122;
            Q122=makeQuery(id+"F2.opPattern","COPY",EDGE,{"derivedFrom":makeQuery(id+"F1.opExtrude","SWEPT_EDGE",EDGE,{"disambiguationData":[OSD([sQuery(id+"F0.wireOp",EDGE,"E1"),sQuery(id+"F0.wireOp",EDGE,"E2")])]}),"instanceName":"3"});
            var Q123;
            Q123=makeQuery(id+"F2.opPattern","COPY",EDGE,{"derivedFrom":makeQuery(id+"F1.opExtrude","CAP_EDGE",EDGE,{"disambiguationData":[OSD([sQuery(id+"F0.wireOp",EDGE,"E7")])],"isStart":false}),"instanceName":"3"});
            var Q124;
            Q124=makeQuery(id+"F1.opExtrude","CAP_EDGE",EDGE,{"disambiguationData":[OSD([sQuery(id+"F0.wireOp",EDGE,"E2")])],"isStart":false});
            var Q125;
            Q125=makeQuery(id+"F1.opExtrude","CAP_EDGE",EDGE,{"disambiguationData":[OSD([sQuery(id+"F0.wireOp",EDGE,"E2")])],"isStart":true});
            fillet(context, id + "F3", {"entities" : qUnion([Q0, Q1, Q2, Q3, Q4, Q5, Q6, Q7, Q8, Q9, Q10, Q11, Q12, Q13, Q14, Q15, Q16, Q17, Q18, Q19, Q20, Q21, Q22, Q23, Q24, Q25, Q26, Q27, Q28, Q29, Q30, Q31, Q32, Q33, Q34, Q35, Q36, Q37, Q38, Q39, Q40, Q41, Q42, Q43, Q44, Q45, Q46, Q47, Q48, Q49, Q50, Q51, Q52, Q53, Q54, Q55, Q56, Q57, Q58, Q59, Q60, Q61, Q62, Q63, Q64, Q65, Q66, Q67, Q68, Q69, Q70, Q71, Q72, Q73, Q74, Q75, Q76, Q77, Q78, Q79, Q80, Q81, Q82, Q83, Q84, Q85, Q86, Q87, Q88, Q89, Q90, Q91, Q92, Q93, Q94, Q95, Q96, Q97, Q98, Q99, Q100, Q101, Q102, Q103, Q104, Q105, Q106, Q107, Q108, Q109, Q110, Q111, Q112, Q113, Q114, Q115, Q116, Q117, Q118, Q119, Q120, Q121, Q122, Q123, Q124, Q125]), "radius" : 2 * mm, "tangentPropagation" : true, "allowEdgeOverflow" : false});
        }
        {
            var Q0;
            Q0=makeQuery(id+"F2.opPattern","COPY",FACE,{"derivedFrom":makeQuery(id+"F1.opExtrude","SWEPT_FACE",FACE,{"disambiguationData":[OSD([sQuery(id+"F0.wireOp",EDGE,"E6")])]}),"instanceName":"1"});
            var sketch = newSketch(context, id + "F4", { "sketchPlane" : qUnion([Q0])});
            skCircle(sketch, "E9", {"center": v(-2.4, -7.14) * mm, "radius": 4.49 * mm});
            skSolve(sketch);
        }
        {
            var Q0;
            {var subQ0=sQuery(id+"F4.wireOp",EDGE,"E9");var subQ1=sQuery(id+"F0.wireOp",EDGE,"E6");var subQ2=makeQuery(id+"F2.opPattern","COPY",FACE,{"derivedFrom":makeQuery(id+"F1.opExtrude","SWEPT_FACE",FACE,{"disambiguationData":[OSD([subQ1])]}),"instanceName":"1"});var subQ5=makeQuery(id+"F3.opFillet","BLEND_EDGE",EDGE,{"blendedFrom":[makeQuery(id+"F2.opPattern","COPY",EDGE,{"derivedFrom":makeQuery(id+"F1.opExtrude","CAP_EDGE",EDGE,{"disambiguationData":[OSD([subQ1])],"isStart":false}),"instanceName":"1"}),subQ2],"blendedInto":[subQ2]});var subQ6=makeQuery(id+"F4.imprint","INTERSECT",VERTEX,{"derivedFrom":[subQ5,subQ0]});Q0=makeQuery(id+"F4.imprint","IMPRINT",FACE,{"disambiguationData":[TD([[makeQuery(id+"F4.imprint","IMPRINT",EDGE,{"disambiguationData":[TD([[subQ6,-1.0]])],"derivedFrom":subQ0}),1.0]])]});}
            var Q1;
            {var subQ0=sQuery(id+"F4.wireOp",EDGE,"E9");var subQ1=sQuery(id+"F0.wireOp",EDGE,"E6");var subQ2=makeQuery(id+"F2.opPattern","COPY",FACE,{"derivedFrom":makeQuery(id+"F1.opExtrude","SWEPT_FACE",FACE,{"disambiguationData":[OSD([subQ1])]}),"instanceName":"1"});var subQ5=makeQuery(id+"F3.opFillet","BLEND_EDGE",EDGE,{"blendedFrom":[makeQuery(id+"F2.opPattern","COPY",EDGE,{"derivedFrom":makeQuery(id+"F1.opExtrude","CAP_EDGE",EDGE,{"disambiguationData":[OSD([subQ1])],"isStart":false}),"instanceName":"1"}),subQ2],"blendedInto":[subQ2]});var subQ6=makeQuery(id+"F4.imprint","INTERSECT",VERTEX,{"derivedFrom":[subQ5,subQ0]});Q1=makeQuery(id+"F4.imprint","IMPRINT",FACE,{"disambiguationData":[TD([[makeQuery(id+"F4.imprint","IMPRINT",EDGE,{"disambiguationData":[TD([[subQ6,1.0]])],"derivedFrom":subQ0}),1.0]])]});}
            extrude(context, id + "F5", {"entities" : qUnion([Q0, Q1]), "operationType" : NewBodyOperationType.REMOVE, "oppositeDirection" : true, "depth" : 25 * mm, "offsetDistance" : 25 * mm, "hasDraft" : true, "draftAngle" : 3 * degree, "hasSecondDirection" : true, "secondDirectionOppositeDirection" : false, "secondDirectionDepth" : 25 * mm});
        }
    });
